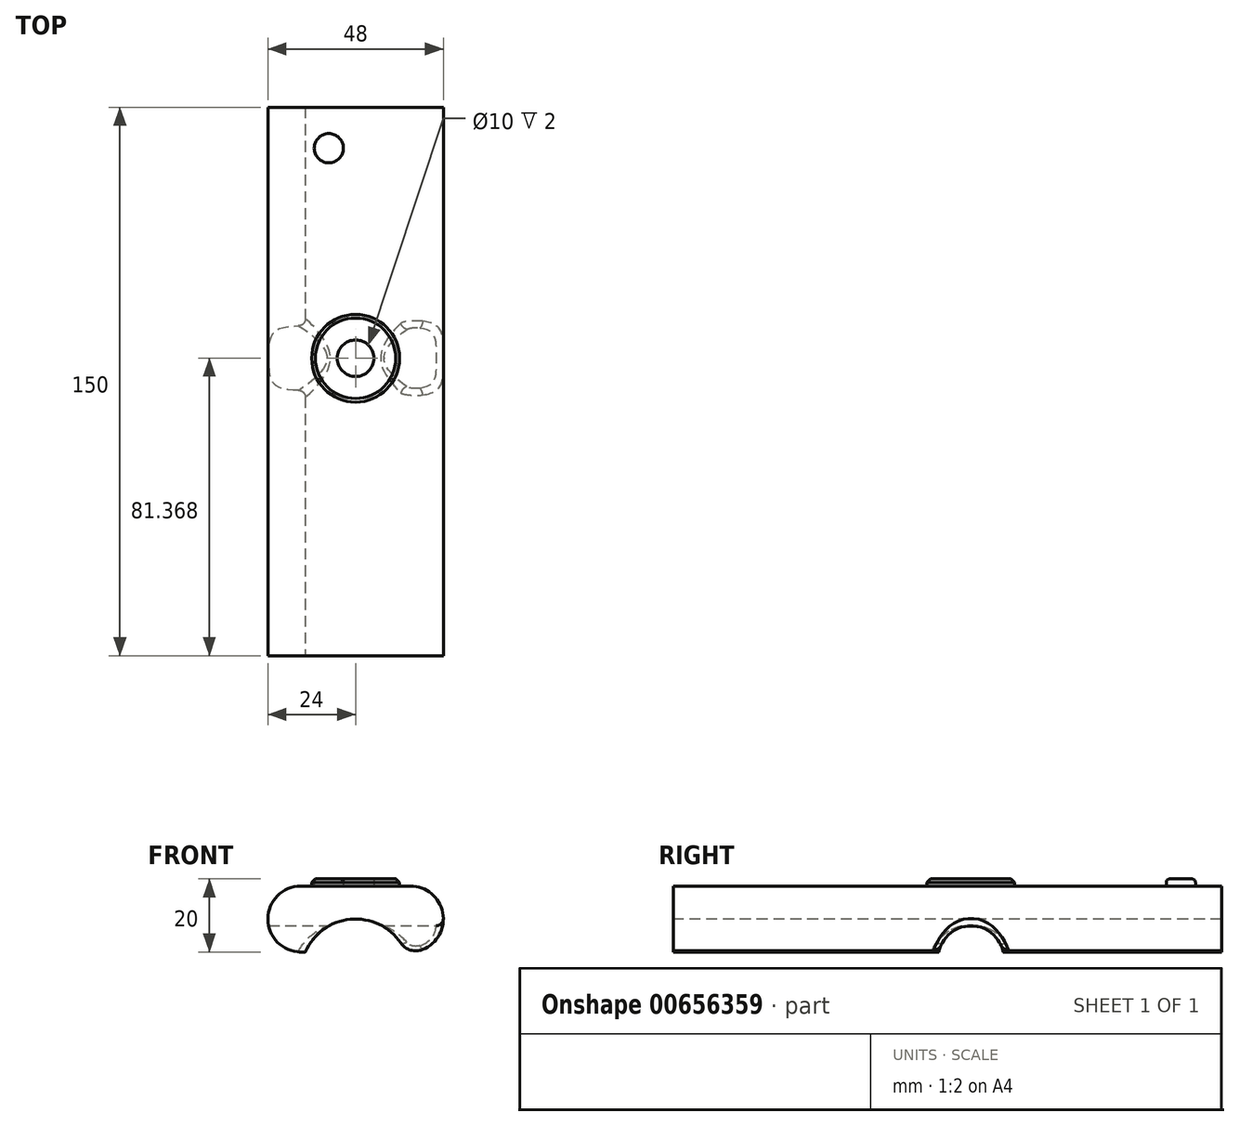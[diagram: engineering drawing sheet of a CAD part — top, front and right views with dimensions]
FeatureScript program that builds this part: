
annotation { "Feature Type Name" : "Feature", "Feature Type Description" : "" }
export const myFeature = defineFeature(function(context is Context, id is Id, definition is map)
    precondition{}
    {
        {
            var Q0;
            Q0=qCreatedBy(makeId("Front.planeOp"),FACE);
            var sketch = newSketch(context, id + "F0", { "sketchPlane" : qUnion([Q0])});
            skLineSegment(sketch, "E0.bottom", {"start": v(15, -9) * mm, "end": v(-15, -9) * mm});
            skLineSegment(sketch, "E0.top", {"start": v(15, 9) * mm, "end": v(-15, 9) * mm});
            skLineSegment(sketch, "E0.left", {"start": v(24, 0) * mm, "end": v(24, 0) * mm});
            skLineSegment(sketch, "E0.right", {"start": v(-24, 0) * mm, "end": v(-24, 0) * mm});
            skPoint(sketch, "E0.middle", {"position": v(0, 0) * mm});
            skPoint(sketch, "E1.visualSharp", {"position": v(-24, 9) * mm});
            skArc(sketch, "E1.filletArc", {"start": v(-15, 9) * mm, "mid": v(-21.36, 6.36) * mm, "end": v(-24, 0) * mm});
            skPoint(sketch, "E2.visualSharp", {"position": v(-24, -9) * mm});
            skArc(sketch, "E2.filletArc", {"start": v(-24, 0) * mm, "mid": v(-21.36, -6.36) * mm, "end": v(-15, -9) * mm});
            skPoint(sketch, "E3.visualSharp", {"position": v(24, -9) * mm});
            skArc(sketch, "E3.filletArc", {"start": v(15, -9) * mm, "mid": v(21.36, -6.36) * mm, "end": v(24, 0) * mm});
            skPoint(sketch, "E4.visualSharp", {"position": v(24, 9) * mm});
            skArc(sketch, "E4.filletArc", {"start": v(24, 0) * mm, "mid": v(21.36, 6.36) * mm, "end": v(15, 9) * mm});
            skSolve(sketch);
        }
        {
            var Q0;
            Q0=makeQuery(id+"F0.imprint","IMPRINT",FACE,{"disambiguationData":[TD([[makeQuery(id+"F0.imprint","IMPRINT",EDGE,{"derivedFrom":sQuery(id+"F0.wireOp",EDGE,"E0.bottom")}),-1.0]])]});
            extrude(context, id + "F1", {"entities" : qUnion([Q0]), "oppositeDirection" : true, "depth" : 150 * mm, "offsetDistance" : 25 * mm});
        }
        {
            var Q0;
            Q0=makeQuery(id+"F1.opExtrude","CAP_FACE",FACE,{"disambiguationData":[OSD([sQuery(id+"F0.wireOp",EDGE,"E0.bottom"),sQuery(id+"F0.wireOp",EDGE,"E0.top"),sQuery(id+"F0.wireOp",EDGE,"E1.filletArc"),sQuery(id+"F0.wireOp",EDGE,"E2.filletArc"),sQuery(id+"F0.wireOp",EDGE,"E3.filletArc"),sQuery(id+"F0.wireOp",EDGE,"E4.filletArc")])],"isStart":true});
            var sketch = newSketch(context, id + "F2", { "sketchPlane" : qUnion([Q0])});
            skCircle(sketch, "E5", {"center": v(0, -15) * mm, "radius": 15 * mm});
            skSolve(sketch);
        }
        {
            var Q0;
            {var subQ0=sQuery(id+"F2.wireOp",EDGE,"E5");var subQ1=makeQuery(id+"F1.opExtrude","CAP_EDGE",EDGE,{"disambiguationData":[OSD([sQuery(id+"F0.wireOp",EDGE,"E0.bottom")])],"isStart":true});var subQ2=makeQuery(id+"F2.imprint","INTERSECT",VERTEX,{"disambiguationData":[OD(0.0)],"derivedFrom":[subQ1,subQ0]});Q0=makeQuery(id+"F2.imprint","IMPRINT",FACE,{"disambiguationData":[TD([[makeQuery(id+"F2.imprint","IMPRINT",EDGE,{"disambiguationData":[TD([[subQ2,-1.0]])],"derivedFrom":subQ0}),1.0]])]});}
            extrude(context, id + "F3", {"entities" : qUnion([Q0]), "operationType" : NewBodyOperationType.REMOVE, "oppositeDirection" : true, "depth" : 150 * mm, "offsetDistance" : 25 * mm});
        }
        {
            var Q0;
            {var subQ0=sQuery(id+"F2.wireOp",EDGE,"E5");var subQ1=sQuery(id+"F0.wireOp",EDGE,"E0.bottom");Q0=makeQuery(id+"F3.boolean.opBoolean","COPY",EDGE,{"derivedFrom":makeQuery(id+"F3.opExtrude","SWEPT_EDGE",EDGE,{"disambiguationData":[OSD([subQ1,subQ0]),TDD([makeQuery(id+"F2.imprint","INTERSECT",VERTEX,{"disambiguationData":[OD(1.0)],"derivedFrom":[makeQuery(id+"F1.opExtrude","CAP_EDGE",EDGE,{"disambiguationData":[OSD([subQ1])],"isStart":true}),subQ0]})])]})});}
            var Q1;
            {var subQ0=sQuery(id+"F2.wireOp",EDGE,"E5");var subQ1=sQuery(id+"F0.wireOp",EDGE,"E0.bottom");Q1=makeQuery(id+"F3.boolean.opBoolean","COPY",EDGE,{"derivedFrom":makeQuery(id+"F3.opExtrude","SWEPT_EDGE",EDGE,{"disambiguationData":[OSD([subQ1,subQ0]),TDD([makeQuery(id+"F2.imprint","INTERSECT",VERTEX,{"disambiguationData":[OD(0.0)],"derivedFrom":[makeQuery(id+"F1.opExtrude","CAP_EDGE",EDGE,{"disambiguationData":[OSD([subQ1])],"isStart":true}),subQ0]})])]})});}
            fillet(context, id + "F4", {"entities" : qUnion([Q0, Q1]), "radius" : 5 * mm, "tangentPropagation" : true, "allowEdgeOverflow" : false});
        }
        {
            var Q0;
            Q0=makeQuery(id+"F1.opExtrude","SWEPT_FACE",FACE,{"disambiguationData":[OSD([sQuery(id+"F0.wireOp",EDGE,"E0.top")])]});
            var sketch = newSketch(context, id + "F5", { "sketchPlane" : qUnion([Q0])});
            skCircle(sketch, "E6", {"center": v(0, 81.37) * mm, "radius": 12 * mm});
            skCircle(sketch, "E7", {"center": v(0, 81.37) * mm, "radius": 5 * mm});
            skSolve(sketch);
        }
        {
            var Q0;
            Q0=makeQuery(id+"F5.imprint","IMPRINT",FACE,{"disambiguationData":[TD([[makeQuery(id+"F5.imprint","IMPRINT",EDGE,{"derivedFrom":sQuery(id+"F5.wireOp",EDGE,"E6")}),1.0]])]});
            extrude(context, id + "F6", {"entities" : qUnion([Q0]), "operationType" : NewBodyOperationType.ADD, "depth" : 2 * mm, "offsetDistance" : 25 * mm});
        }
        {
            var Q0;
            Q0=makeQuery(id+"F6.opExtrude","CAP_EDGE",EDGE,{"disambiguationData":[OSD([sQuery(id+"F5.wireOp",EDGE,"E6")])],"isStart":false});
            chamfer(context, id + "F7", {"entities" : qUnion([Q0]), "width" : 1 * mm, "tangentPropagation" : true});
        }
        {
            var Q0;
            Q0=qCreatedBy(makeId("Right.planeOp"),FACE);
            var sketch = newSketch(context, id + "F8", { "sketchPlane" : qUnion([Q0])});
            skCircle(sketch, "E8", {"center": v(81.42, -10.86) * mm, "radius": 9 * mm});
            skSolve(sketch);
        }
        {
            var Q0;
            Q0=makeQuery(id+"F8.imprint","IMPRINT",FACE,{"disambiguationData":[TD([[makeQuery(id+"F8.imprint","IMPRINT",EDGE,{"derivedFrom":sQuery(id+"F8.wireOp",EDGE,"E8")}),1.0]])]});
            extrude(context, id + "F9", {"entities" : qUnion([Q0]), "operationType" : NewBodyOperationType.REMOVE, "endBound" : BoundingType.SYMMETRIC, "oppositeDirection" : true, "depth" : 50 * mm, "offsetDistance" : 25 * mm});
        }
        {
            var Q0;
            Q0=makeQuery(id+"F9.boolean.opBoolean","INTERSECT",EDGE,{"disambiguationData":[OD(0.0)],"derivedFrom":[makeQuery(id+"F3.boolean.opBoolean","COPY",FACE,{"derivedFrom":makeQuery(id+"F3.opExtrude","SWEPT_FACE",FACE,{"disambiguationData":[OSD([sQuery(id+"F2.wireOp",EDGE,"E5")])]})}),makeQuery(id+"F9.opExtrude","SWEPT_FACE",FACE,{"disambiguationData":[OSD([sQuery(id+"F8.wireOp",EDGE,"E8")])]})]});
            var Q1;
            Q1=makeQuery(id+"F9.boolean.opBoolean","INTERSECT",EDGE,{"derivedFrom":[makeQuery(id+"F1.opExtrude","SWEPT_FACE",FACE,{"disambiguationData":[OSD([sQuery(id+"F0.wireOp",EDGE,"E3.filletArc"),sQuery(id+"F0.wireOp",EDGE,"E4.filletArc")])]}),makeQuery(id+"F9.opExtrude","SWEPT_FACE",FACE,{"disambiguationData":[OSD([sQuery(id+"F8.wireOp",EDGE,"E8")])]})]});
            fillet(context, id + "F10", {"entities" : qUnion([Q0, Q1]), "radius" : 2 * mm, "tangentPropagation" : true, "allowEdgeOverflow" : false});
        }
        {
            var Q0;
            {var subQ4=sQuery(id+"F0.wireOp",EDGE,"E0.top");Q0=makeQuery(id+"F6.boolean.opBoolean","SPLIT",FACE,{"disambiguationData":[TD([makeQuery(id+"F6.opExtrude","SWEPT_FACE",FACE,{"disambiguationData":[OSD([sQuery(id+"F5.wireOp",EDGE,"E6")])]})])],"derivedFrom":makeQuery(id+"F1.opExtrude","SWEPT_FACE",FACE,{"disambiguationData":[OSD([subQ4])]})});}
            var sketch = newSketch(context, id + "F11", { "sketchPlane" : qUnion([Q0])});
            skCircle(sketch, "E9", {"center": v(-7.33, 138.81) * mm, "radius": 4 * mm});
            skSolve(sketch);
        }
        {
            var Q0;
            Q0=makeQuery(id+"F11.imprint","IMPRINT",FACE,{"disambiguationData":[TD([[makeQuery(id+"F11.imprint","IMPRINT",EDGE,{"derivedFrom":sQuery(id+"F11.wireOp",EDGE,"E9")}),1.0]])]});
            extrude(context, id + "F12", {"entities" : qUnion([Q0]), "operationType" : NewBodyOperationType.ADD, "depth" : 2 * mm, "offsetDistance" : 25 * mm});
        }
        {
            var Q0;
            Q0=makeQuery(id+"F12.opExtrude","CAP_EDGE",EDGE,{"disambiguationData":[OSD([sQuery(id+"F11.wireOp",EDGE,"E9")])],"isStart":false});
            fillet(context, id + "F13", {"entities" : qUnion([Q0]), "radius" : 1 * mm, "tangentPropagation" : true, "allowEdgeOverflow" : false});
        }
    });
